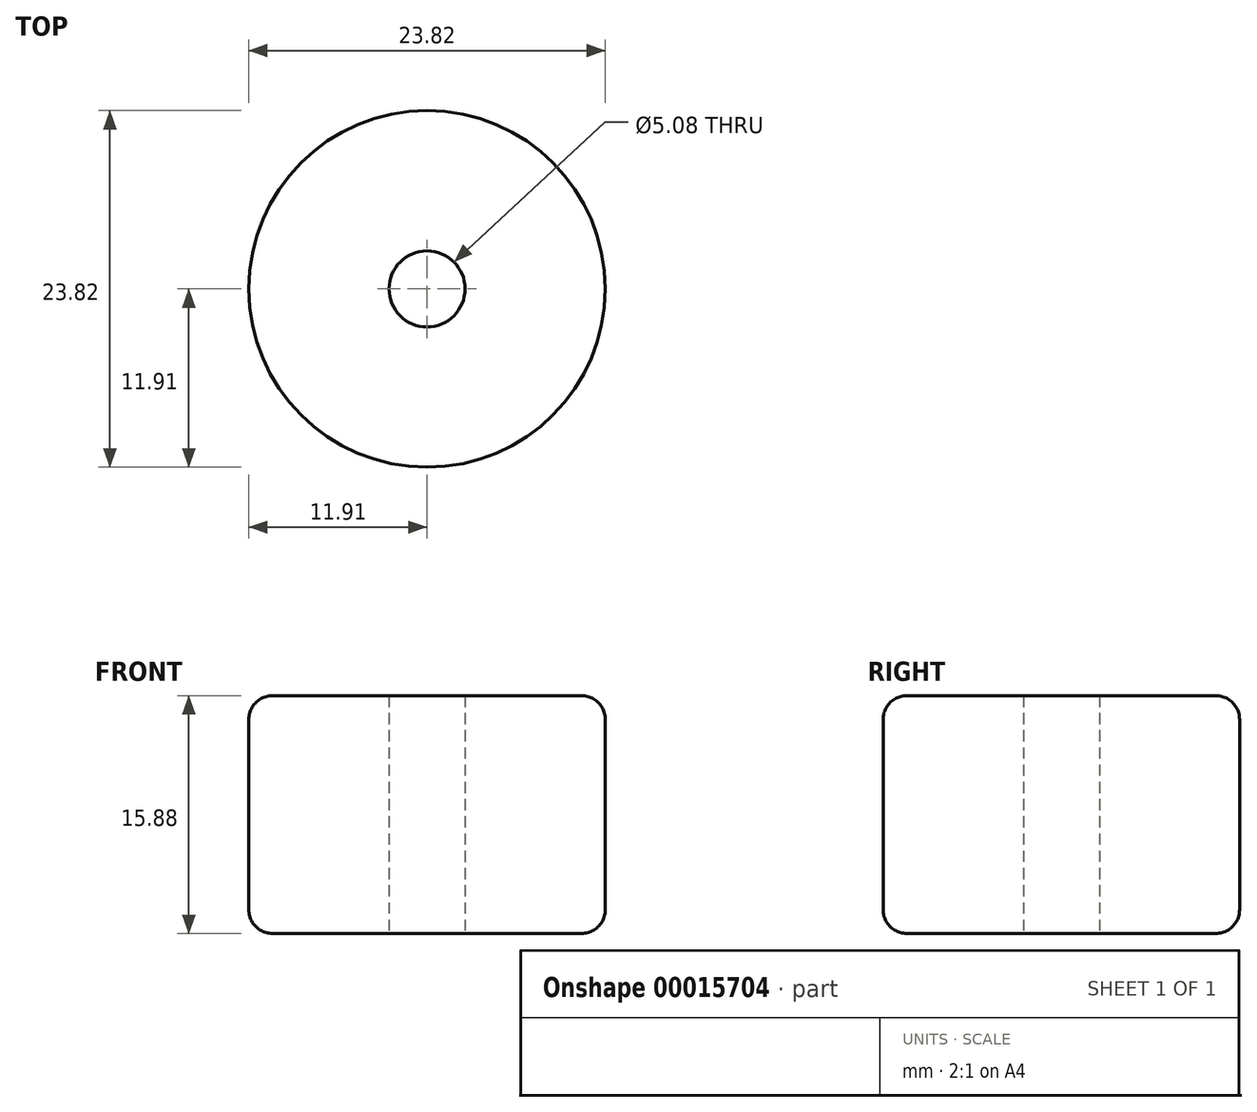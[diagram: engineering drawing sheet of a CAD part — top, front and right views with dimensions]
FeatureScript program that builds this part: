
annotation { "Feature Type Name" : "Feature", "Feature Type Description" : "" }
export const myFeature = defineFeature(function(context is Context, id is Id, definition is map)
    precondition{}
    {
        {
            var Q0;
            Q0=qCreatedBy(makeId("Top.planeOp"),FACE);
            var sketch = newSketch(context, id + "F0", { "sketchPlane" : qUnion([Q0])});
            skCircle(sketch, "E0", {"center": v(0, 0) * mm, "radius": 11.9 * mm});
            skCircle(sketch, "E1", {"center": v(0, 0) * mm, "radius": 2.54 * mm});
            skSolve(sketch);
        }
        {
            var Q0;
            Q0 = qSketchRegion(id + "F0", true);
            extrude(context, id + "F1", {"entities" : qUnion([Q0]), "depth" : 15.88 * mm});
        }
        {
            var Q0;
            Q0=makeQuery(id+"F1.opExtrude","CAP_EDGE",EDGE,{"disambiguationData":[OSD([sQuery(id+"F0.wireOp",EDGE,"E0")])],"isStart":false});
            var Q1;
            Q1=makeQuery(id+"F1.opExtrude","CAP_EDGE",EDGE,{"disambiguationData":[OSD([sQuery(id+"F0.wireOp",EDGE,"E0")])],"isStart":true});
            fillet(context, id + "F2", {"entities" : qUnion([Q0, Q1]), "radius" : 1.59 * mm, "tangentPropagation" : true, "allowEdgeOverflow" : false});
        }
    });
